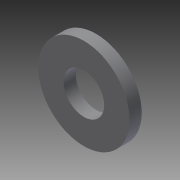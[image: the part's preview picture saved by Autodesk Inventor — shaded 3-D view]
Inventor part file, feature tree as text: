
AUTODESK INVENTOR PART (.ipt)
format: ipt  version: 2014 SP2 (Build 180246200, 246)  size: 93,184 bytes
history: native  units: in
note: dims shown in document units (in); Inventor stores cm internally (conversion verified against a paired STEP export)
features: other x7, revolve x1, sketch x1
ambient origin geometry x8: Origin, YZ Plane, XZ Plane, XY Plane, X Axis, Y Axis, Z Axis, Center Point
bodies: Solid1 (feature_tree)
feature tree (9):
  revolve  "Revolution1"  [1 undecoded]
  other  "part_to_rod_XY"
  other  "part_to_rod_YZ"
  other  "part_to_rod_ZX"
  other  "part_to_rod_X"
  other  "part_to_rod_Y"
  other  "part_to_rod_Z"
  other  "part_to_rod_Center"
  sketch  "Sketch_1"  dims[d0=360.0deg]
note: 1 required parameter value undecoded (feature->parameter linkage not recoverable at this tier; creation-order binding heuristic only, values carry confidence <= 0.55)
